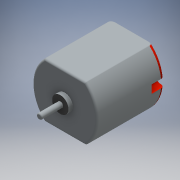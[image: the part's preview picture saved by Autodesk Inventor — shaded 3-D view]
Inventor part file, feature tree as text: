
AUTODESK INVENTOR PART (.ipt)
format: ipt  version: 2016 (Build 200138000, 138)  size: 299,520 bytes
history: native  units: mm
features: extrude x7, sketch x7, fillet x5, other x1, mirror x1
ambient origin geometry x8: Origin, YZ Plane, XZ Plane, XY Plane, X Axis, Y Axis, Z Axis, Center Point
bodies: Body1 (feature_tree)
feature tree (21):
  other  "Sólido1"
  extrude  "Extrusión1"  Depth=4.8mm TaperAngle=0.0deg
  extrude  "Extrusión2"  Depth=2.4mm TaperAngle=0.0deg
  mirror  "Simetría1"
  extrude  "Extrusión3"  Depth=1.6mm TaperAngle=0.0deg
  extrude  "Extrusión4"  Depth=0.4mm
  extrude  "Extrusión5"  Depth=0.7mm
  extrude  "Extrusión6"  Depth=0.4mm
  extrude  "Extrusión7"  [1 undecoded]
  fillet  "Empalme1"  [1 undecoded]
  fillet  "Empalme2"  [1 undecoded]
  fillet  "Empalme3"  [1 undecoded]
  fillet  "Empalme4"  [1 undecoded]
  fillet  "Empalme5"  [1 undecoded]
  sketch  "Boceto1"  dims[d7=20.0mm d8=0.0mm d23=4.8mm d24=0.0mm]
  sketch  "Boceto3"  dims[d29=1.6mm d30=0.0mm d37=2.4mm d38=0.0mm]
  sketch  "Boceto6"  dims[d39=3.1mm d40=0.0mm d43=1.6mm d44=0.0mm]
  sketch  "Boceto7"  dims[d45=9.4mm d46=0.0mm d47=0.4mm]
  sketch  "Boceto8"  dims[d48=0.4mm d49=0.7mm]
  sketch  "Boceto9"  dims[d50=1.3mm d51=0.4mm]
  sketch  "Boceto10"
note: 6 required parameter values undecoded (feature->parameter linkage not recoverable at this tier; creation-order binding heuristic only, values carry confidence <= 0.55)
